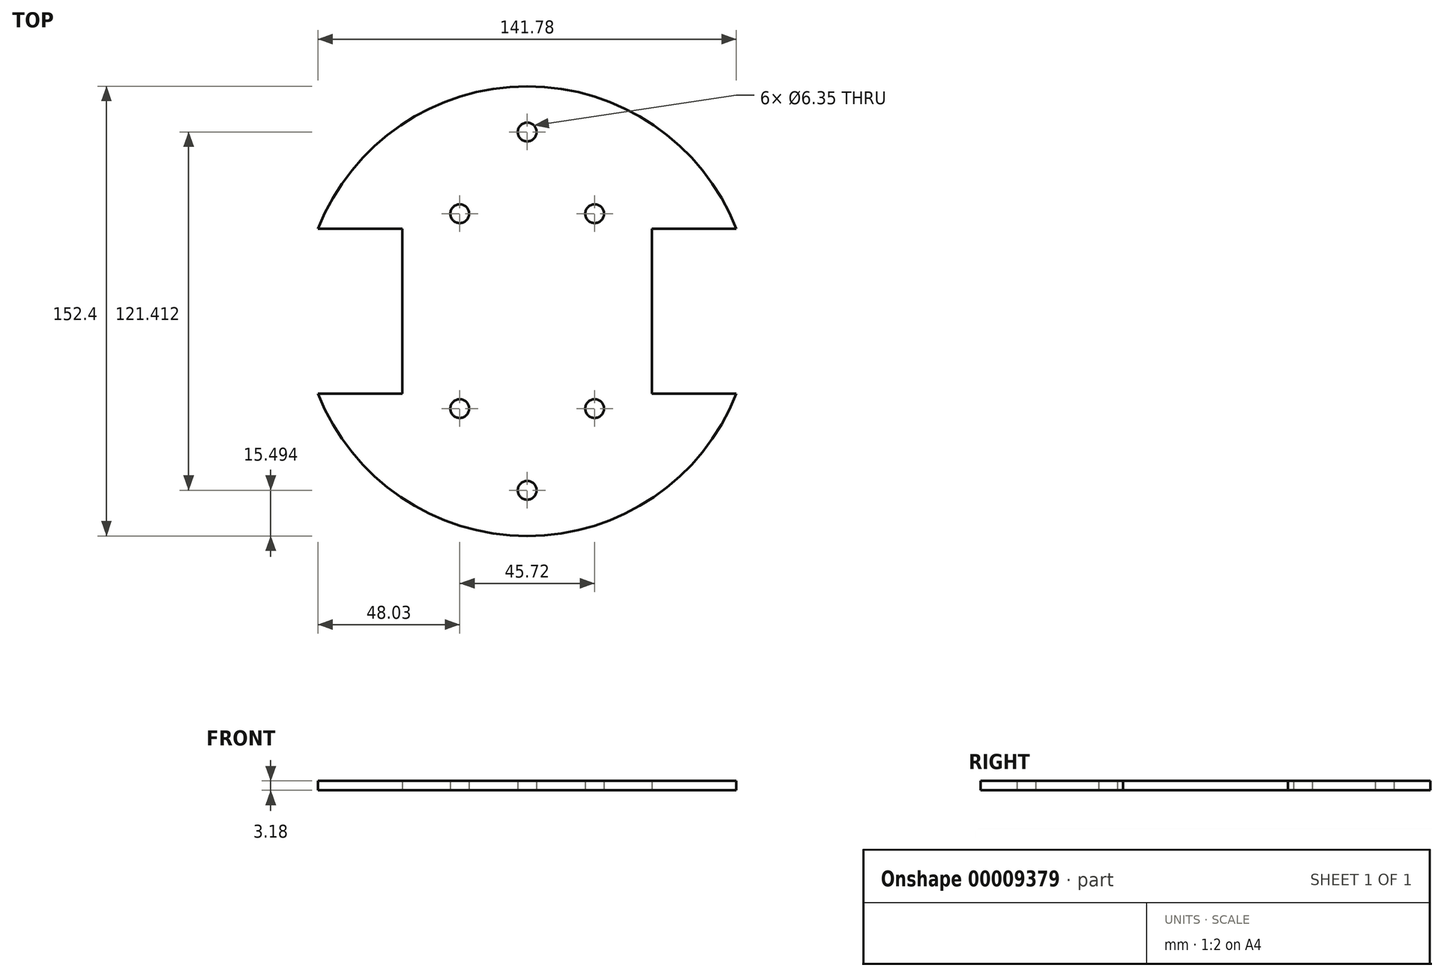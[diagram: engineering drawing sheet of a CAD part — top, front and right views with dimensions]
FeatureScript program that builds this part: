
annotation { "Feature Type Name" : "Feature", "Feature Type Description" : "" }
export const myFeature = defineFeature(function(context is Context, id is Id, definition is map)
    precondition{}
    {
        {
            var Q0;
            Q0=qCreatedBy(makeId("Top.planeOp"),FACE);
            var sketch = newSketch(context, id + "F0", { "sketchPlane" : qUnion([Q0])});
            skCircle(sketch, "E0", {"center": v(0, 0) * mm, "radius": 76.2 * mm});
            skLineSegment(sketch, "E1", {"start": v(-42.32, 27.94) * mm, "end": v(-70.9, 27.94) * mm});
            skLineSegment(sketch, "E2", {"start": v(-42.32, -27.94) * mm, "end": v(-70.9, -27.94) * mm});
            skLineSegment(sketch, "E3", {"start": v(42.32, -27.94) * mm, "end": v(70.9, -27.94) * mm});
            skLineSegment(sketch, "E4", {"start": v(42.32, 27.94) * mm, "end": v(70.9, 27.94) * mm});
            skCircle(sketch, "E5", {"center": v(0, 60.7) * mm, "radius": 3.18 * mm});
            skCircle(sketch, "E6", {"center": v(0, -60.7) * mm, "radius": 3.18 * mm});
            skCircle(sketch, "E7", {"center": v(22.86, 33.02) * mm, "radius": 3.18 * mm});
            skCircle(sketch, "E8", {"center": v(-22.86, 33.02) * mm, "radius": 3.18 * mm});
            skCircle(sketch, "E9", {"center": v(-22.86, -33.02) * mm, "radius": 3.18 * mm});
            skCircle(sketch, "E10", {"center": v(22.86, -33.02) * mm, "radius": 3.18 * mm});
            skLineSegment(sketch, "E11", {"start": v(42.32, 27.94) * mm, "end": v(42.32, -27.94) * mm});
            skLineSegment(sketch, "E12", {"start": v(-42.32, 27.94) * mm, "end": v(-42.32, -27.94) * mm});
            skSolve(sketch);
        }
        {
            var Q0;
            {var subQ0=sQuery(id+"F0.wireOp",EDGE,"E1");Q0=makeQuery(id+"F0.imprint","IMPRINT",FACE,{"disambiguationData":[TD([[makeQuery(id+"F0.imprint","IMPRINT",EDGE,{"derivedFrom":subQ0}),-1.0]])]});}
            var Q1;
            Q1=makeQuery(id+"F0.imprint","IMPRINT",FACE,{"disambiguationData":[TD([[makeQuery(id+"F0.imprint","IMPRINT",EDGE,{"derivedFrom":sQuery(id+"F0.wireOp",EDGE,"E5")}),-1.0]])]});
            var Q2;
            {var subQ0=sQuery(id+"F0.wireOp",EDGE,"E2");Q2=makeQuery(id+"F0.imprint","IMPRINT",FACE,{"disambiguationData":[TD([[makeQuery(id+"F0.imprint","IMPRINT",EDGE,{"derivedFrom":subQ0}),1.0]])]});}
            var Q3;
            {var subQ0=sQuery(id+"F0.wireOp",EDGE,"E3");Q3=makeQuery(id+"F0.imprint","IMPRINT",FACE,{"disambiguationData":[TD([[makeQuery(id+"F0.imprint","IMPRINT",EDGE,{"derivedFrom":subQ0}),-1.0]])]});}
            var Q4;
            {var subQ0=sQuery(id+"F0.wireOp",EDGE,"E4");Q4=makeQuery(id+"F0.imprint","IMPRINT",FACE,{"disambiguationData":[TD([[makeQuery(id+"F0.imprint","IMPRINT",EDGE,{"derivedFrom":subQ0}),1.0]])]});}
            var Q5;
            {var subQ7=sQuery(id+"F0.wireOp",EDGE,"508fb9b8-fbcc-49e6-b67b-15da42e41a79.rect.bottom");var subQ9=sQuery(id+"F0.wireOp",EDGE,"E7");var subQ12=makeQuery(id+"F0.imprint","INTERSECT",VERTEX,{"derivedFrom":[subQ7,subQ9]});Q5=makeQuery(id+"F0.imprint","IMPRINT",FACE,{"disambiguationData":[TD([[makeQuery(id+"F0.imprint","IMPRINT",EDGE,{"disambiguationData":[TD([[subQ12,-1.0]])],"derivedFrom":subQ7}),1.0]])]});}
            extrude(context, id + "F1", {"entities" : qUnion([Q0, Q1, Q2, Q3, Q4, Q5]), "depth" : 3.17 * mm});
        }
    });
